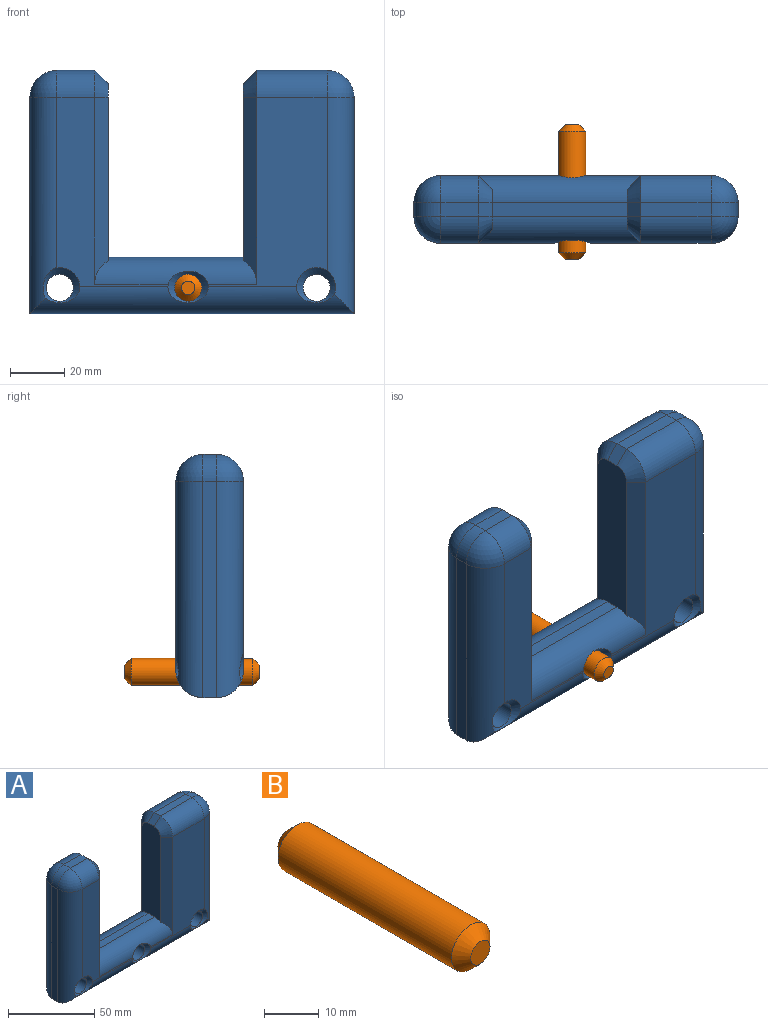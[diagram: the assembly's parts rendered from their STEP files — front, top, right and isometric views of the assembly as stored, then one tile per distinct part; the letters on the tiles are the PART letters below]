
ASSEMBLY  parts=2 mates=1
PART A: 46 faces, bbox 120x25x90 mm
  f0: plane 70x41.21mm, normal (0,-1,0), area 952.4mm2, adj f16,f17,f25,f27,f28,f35,f45
  f1: plane 70x46.6mm, normal (0,1,0), area 1809.1mm2, adj f9,f10,f20,f24,f26,f34,f36
  f2: plane 26.05x5mm, normal (0,0,1), area 130.3mm2, adj f18,f19,f20,f38
  f3: plane 65.46x15mm, normal (-1,0,0), area 955.5mm2, adj f4,f34,f35,f36,f37,f38,f39,f40
  f4: plane 50x5mm, normal (0,0,1), area 250mm2, adj f3,f5,f34,f35
  f5: plane 65.46x15mm, normal (1,0,0), area 955.5mm2, adj f4,f34,f35,f41,f42,f43,f44,f45
  f6: plane 13.95x5mm, normal (0,0,1), area 69.7mm2, adj f27,f30,f33,f43
  f7: plane 80x5mm, normal (-1,0,0), area 400mm2, adj f8,f28,f29,f33
  f8: plane 120x5mm, normal (0,0,-1), area 600mm2, adj f7,f11,f25,f26
  f9: cylinder r=5mm len=22.5mm, axis (0,1,0), area 689.1mm2, adj f1,f14,f16,f26,f34
  f10: cylinder r=5mm len=22.5mm, axis (0,1,0), area 693.5mm2, adj f1,f15,f24,f26
  f11: plane 80x5mm, normal (1,0,0), area 400mm2, adj f8,f19,f23,f24
  f12: cylinder r=5mm len=22.5mm, axis (0,1,0), area 689.4mm2, adj f14,f17,f26,f29
  f13: plane 70x44.04mm, normal (0,-1,0), area 1773.1mm2, adj f15,f16,f18,f23,f25,f35,f40
  f14: plane 70x43.78mm, normal (0,1,0), area 980.6mm2, adj f9,f12,f26,f29,f30,f34,f41
  f15: cone r=5mm half-angle=45deg, axis (0,-1,0), area 100.4mm2, adj f10,f13,f23,f25
  f16: cone r=5mm half-angle=45deg, axis (0,-1,0), area 85.2mm2, adj f0,f9,f13,f25,f35
  f17: cone r=5mm half-angle=45deg, axis (0,-1,0), area 88.6mm2, adj f0,f12,f25,f28
  f18: cylinder r=10mm len=26.05mm, axis (1,0,0), area 409.2mm2, adj f2,f13,f21,f39
  f19: cylinder r=10mm len=10mm, axis (0,1,0), area 78.5mm2, adj f2,f11,f21,f22
  f20: cylinder r=10mm len=26.05mm, axis (-1,0,0), area 409.2mm2, adj f1,f2,f22,f37
  f21: sphere r=10mm, area 157.1mm2, adj f18,f19,f23
  f22: sphere r=10mm, area 157.1mm2, adj f19,f20,f24
  f23: cylinder r=10mm len=80mm, axis (0,0,-1), area 1181.7mm2, adj f11,f13,f15,f21,f25
  f24: cylinder r=10mm len=80mm, axis (0,0,1), area 1197mm2, adj f1,f10,f11,f22,f26
  f25: cylinder r=10mm len=120mm, axis (-1,0,0), area 1567.4mm2, adj f0,f8,f13,f15,f16,f17,f23,f28
  f26: cylinder r=10mm len=120mm, axis (1,0,0), area 1640.2mm2, adj f1,f8,f9,f10,f12,f14,f24,f29
  f27: cylinder r=10mm len=13.95mm, axis (1,0,0), area 219.1mm2, adj f0,f6,f31,f44
  f28: cylinder r=10mm len=80mm, axis (0,0,1), area 1160mm2, adj f0,f7,f17,f25,f31
  f29: cylinder r=10mm len=80mm, axis (0,0,-1), area 1179.6mm2, adj f7,f12,f14,f26,f32
  f30: cylinder r=10mm len=13.95mm, axis (-1,0,0), area 219.1mm2, adj f6,f14,f32,f42
  f31: sphere r=10mm, area 157.1mm2, adj f27,f28,f33
  f32: sphere r=10mm, area 157.1mm2, adj f29,f30,f33
  f33: cylinder r=10mm len=10mm, axis (0,-1,0), area 78.5mm2, adj f6,f7,f31,f32
  f34: cylinder r=10mm len=60mm, axis (-1,0,0), area 827.7mm2, adj f1,f3,f4,f5,f9,f14,f36,f41
  f35: cylinder r=10mm len=60mm, axis (1,0,0), area 797.7mm2, adj f0,f3,f4,f5,f13,f16,f40,f45
  f36: plane 69.12x5mm, normal (-0.71,0.71,0), area 445.3mm2, adj f1,f3,f34,f37
  f37: cone r=5mm half-angle=45deg, axis (1,0,0), area 83.3mm2, adj f3,f20,f36,f38
  f38: plane 5x5mm, normal (-0.71,0,0.71), area 35.4mm2, adj f2,f3,f37,f39
  f39: cone r=5mm half-angle=45deg, axis (1,0,0), area 83.3mm2, adj f3,f18,f38,f40
  f40: plane 69.12x5mm, normal (-0.71,-0.71,0), area 445.3mm2, adj f3,f13,f35,f39
  f41: plane 69.12x5mm, normal (0.71,0.71,0), area 445.3mm2, adj f5,f14,f34,f42
  f42: cone r=5mm half-angle=45deg, axis (-1,0,0), area 83.3mm2, adj f5,f30,f41,f43
  f43: plane 5x5mm, normal (0.71,0,0.71), area 35.4mm2, adj f5,f6,f42,f44
  f44: cone r=5mm half-angle=45deg, axis (-1,0,0), area 83.3mm2, adj f5,f27,f43,f45
  f45: plane 69.12x5mm, normal (0.71,-0.71,0), area 445.3mm2, adj f0,f5,f35,f44
PART B: 5 faces, bbox 10x50x10 mm
  f0: cylinder r=5mm len=45mm, axis (0,1,0), area 1413.7mm2, adj f3,f4
  f1: plane 5x5mm, normal (0,-1,0), area 19.6mm2, adj f4
  f2: plane 5x5mm, normal (0,1,0), area 19.6mm2, adj f3
  f3: cone r=5mm half-angle=45deg, axis (0,-1,0), area 83.3mm2, adj f0,f2
  f4: cone r=2.5mm half-angle=45deg, axis (0,1,0), area 83.3mm2, adj f0,f1
PLACE A at identity
PLACE B t=(5.68,19.05,-35.54)mm
MATE slider B.f0 <-> A.f9  axis (0,-1,0) through (5.68,-30.95,-35.54)mm
